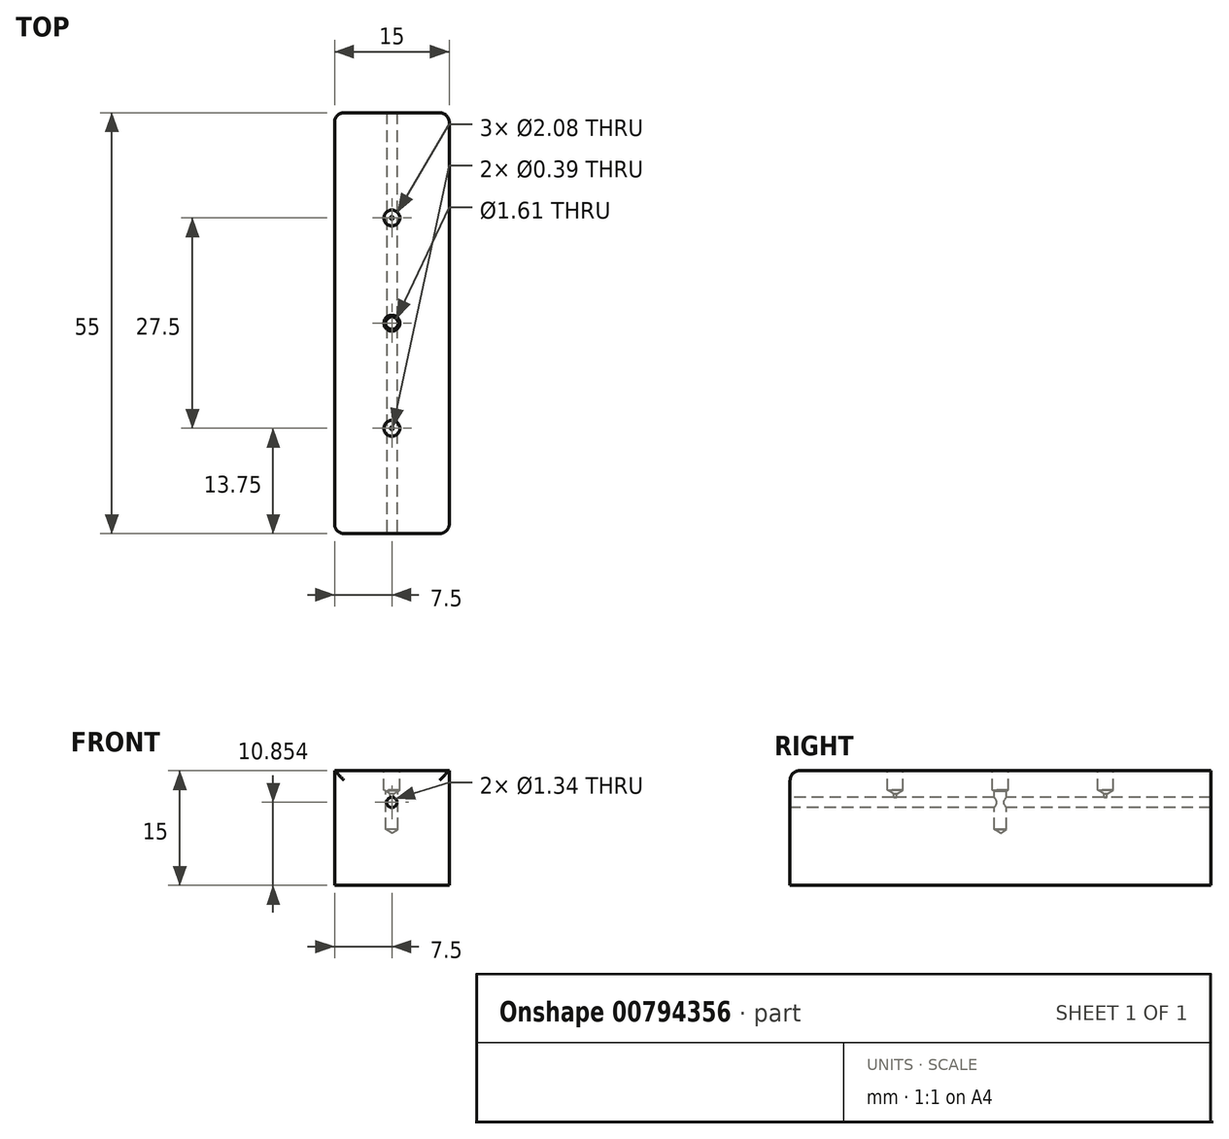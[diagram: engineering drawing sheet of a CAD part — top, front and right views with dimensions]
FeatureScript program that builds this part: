
annotation { "Feature Type Name" : "Feature", "Feature Type Description" : "" }
export const myFeature = defineFeature(function(context is Context, id is Id, definition is map)
    precondition{}
    {
        {
            var Q0;
            Q0=qCreatedBy(makeId("Front.planeOp"),FACE);
            var sketch = newSketch(context, id + "F0", { "sketchPlane" : qUnion([Q0])});
            skLineSegment(sketch, "E0.bottom", {"start": v(-15, 15) * mm, "end": v(0, 15) * mm});
            skLineSegment(sketch, "E0.top", {"start": v(-15, 0) * mm, "end": v(0, 0) * mm});
            skLineSegment(sketch, "E0.left", {"start": v(-15, 15) * mm, "end": v(-15, 0) * mm});
            skLineSegment(sketch, "E0.right", {"start": v(0, 15) * mm, "end": v(0, 0) * mm});
            skSolve(sketch);
        }
        {
            var Q0;
            Q0=makeQuery(id+"F0.imprint","IMPRINT",FACE,{"disambiguationData":[TD([[makeQuery(id+"F0.imprint","IMPRINT",EDGE,{"derivedFrom":sQuery(id+"F0.wireOp",EDGE,"E0.bottom")}),-1.0]])]});
            extrude(context, id + "F1", {"entities" : qUnion([Q0]), "depth" : 55 * mm, "offsetDistance" : 25 * mm});
        }
        {
            var Q0;
            Q0=makeQuery(id+"F1.opExtrude","SWEPT_FACE",FACE,{"disambiguationData":[OSD([sQuery(id+"F0.wireOp",EDGE,"E0.bottom")])]});
            var sketch = newSketch(context, id + "F2", { "sketchPlane" : qUnion([Q0])});
            skLineSegment(sketch, "E1", {"start": v(-7.5, -55) * mm, "end": v(-7.5, 0) * mm});
            skLineSegment(sketch, "E2", {"start": v(-15, -27.5) * mm, "end": v(0, -27.5) * mm});
            skLineSegment(sketch, "E3", {"start": v(-15, -55) * mm, "end": v(-15, -27.5) * mm});
            skLineSegment(sketch, "E4", {"start": v(0, -55) * mm, "end": v(0, -27.5) * mm});
            skLineSegment(sketch, "E5", {"start": v(-15, -27.5) * mm, "end": v(-15, 0) * mm});
            skLineSegment(sketch, "E6", {"start": v(-15, 0) * mm, "end": v(0, 0) * mm});
            skLineSegment(sketch, "E7", {"start": v(0, 0) * mm, "end": v(0, -27.5) * mm});
            skLineSegment(sketch, "E8", {"start": v(-15, -41.25) * mm, "end": v(0, -41.25) * mm});
            skLineSegment(sketch, "E9", {"start": v(-15, -13.75) * mm, "end": v(0, -13.75) * mm});
            skCircle(sketch, "E10", {"center": v(-7.5, -41.25) * mm, "radius": 0.9 * mm});
            skCircle(sketch, "E11", {"center": v(-7.5, -27.5) * mm, "radius": 0.9 * mm});
            skCircle(sketch, "E12", {"center": v(-7.5, -13.75) * mm, "radius": 0.9 * mm});
            skSolve(sketch);
        }
        {
            var Q0;
            Q0=sQuery(id+"F2.wireOp",VERTEX,"E10.center");
            var Q1;
            Q1=sQuery(id+"F2.wireOp",VERTEX,"E11.center");
            var Q2;
            Q2=sQuery(id+"F2.wireOp",VERTEX,"E12.center");
            var Q3;
            Q3=makeQuery(id+"F1.opExtrude","SWEPT_BODY",BODY,{"disambiguationData":[OSD([sQuery(id+"F0.wireOp",EDGE,"E0.bottom"),sQuery(id+"F0.wireOp",EDGE,"E0.top"),sQuery(id+"F0.wireOp",EDGE,"E0.left"),sQuery(id+"F0.wireOp",EDGE,"E0.right")])]});
            hole(context, id + "F3", {"style" : HoleStyle.SIMPLE, "endStyle" : HoleEndStyle.BLIND, "standardTappedOrClearance" : lookupTablePath({ "standard" : "ANSI", "engagement" : "75%", "pitch" : "56 tpi", "size" : "#3", "type" : "Tapped" }), "standardBlindInLast" : lookupTablePath({ "standard" : "ANSI", "engagement" : "75%", "pitch" : "56 tpi", "size" : "#3", "type" : "Tapped" }), "holeDiameter" : 2.08 * mm, "majorDiameter" : 2.5 * mm, "showTappedDepth" : true, "holeDepth" : 2.54 * mm, "isTappedThrough" : true, "tappedDepth" : 1.18 * mm, "tapClearance" : 3, "locations" : qUnion([Q0, Q1, Q2]), "scope" : qUnion([Q3])});
        }
        {
            var Q0;
            Q0=sQuery(id+"F2.wireOp",VERTEX,"E11.center");
            var Q1;
            Q1=sQuery(id+"F2.wireOp",VERTEX,"E12.center");
            var Q2;
            Q2=sQuery(id+"F2.wireOp",VERTEX,"E10.center");
            var Q3;
            Q3=makeQuery(id+"F1.opExtrude","SWEPT_BODY",BODY,{"disambiguationData":[OSD([sQuery(id+"F0.wireOp",EDGE,"E0.bottom"),sQuery(id+"F0.wireOp",EDGE,"E0.top"),sQuery(id+"F0.wireOp",EDGE,"E0.left"),sQuery(id+"F0.wireOp",EDGE,"E0.right")])]});
            hole(context, id + "F4", {"style" : HoleStyle.SIMPLE, "endStyle" : HoleEndStyle.BLIND, "holeDiameter" : 0.4 * mm, "majorDiameter" : 2.5 * mm, "holeDepth" : 0.89 * mm, "isTappedThrough" : true, "tappedDepth" : 1.18 * mm, "tapClearance" : 3, "locations" : qUnion([Q0, Q1, Q2]), "scope" : qUnion([Q3])});
        }
        {
            var Q0;
            Q0=makeQuery(id+"F1.opExtrude","CAP_FACE",FACE,{"disambiguationData":[OSD([sQuery(id+"F0.wireOp",EDGE,"E0.bottom"),sQuery(id+"F0.wireOp",EDGE,"E0.top"),sQuery(id+"F0.wireOp",EDGE,"E0.left"),sQuery(id+"F0.wireOp",EDGE,"E0.right")])],"isStart":false});
            var sketch = newSketch(context, id + "F5", { "sketchPlane" : qUnion([Q0])});
            skLineSegment(sketch, "E13", {"start": v(-7.5, 15) * mm, "end": v(-7.5, 10.85) * mm});
            skCircle(sketch, "E14", {"center": v(-7.5, 10.85) * mm, "radius": 0.67 * mm});
            skSolve(sketch);
        }
        {
            var Q0;
            Q0=makeQuery(id+"F5.imprint","IMPRINT",FACE,{"disambiguationData":[TD([[makeQuery(id+"F5.imprint","IMPRINT",EDGE,{"derivedFrom":sQuery(id+"F5.wireOp",EDGE,"E14")}),1.0]])]});
            var Q1;
            Q1=sQuery(id+"F5.wireOp",EDGE,"E14");
            extrude(context, id + "F6", {"entities" : qUnion([Q0]), "operationType" : NewBodyOperationType.REMOVE, "surfaceEntities" : qUnion([Q1]), "oppositeDirection" : true, "depth" : 58 * mm, "offsetDistance" : 25 * mm});
        }
        {
            var Q0;
            Q0=makeQuery(id+"F1.opExtrude","CAP_EDGE",EDGE,{"disambiguationData":[OSD([sQuery(id+"F0.wireOp",EDGE,"E0.bottom")])],"isStart":false});
            var Q1;
            Q1=makeQuery(id+"F1.opExtrude","CAP_EDGE",EDGE,{"disambiguationData":[OSD([sQuery(id+"F0.wireOp",EDGE,"E0.right")])],"isStart":true});
            var Q2;
            Q2=makeQuery(id+"F1.opExtrude","CAP_EDGE",EDGE,{"disambiguationData":[OSD([sQuery(id+"F0.wireOp",EDGE,"E0.left")])],"isStart":true});
            var Q3;
            Q3=makeQuery(id+"F1.opExtrude","CAP_EDGE",EDGE,{"disambiguationData":[OSD([sQuery(id+"F0.wireOp",EDGE,"E0.left")])],"isStart":false});
            var Q4;
            Q4=makeQuery(id+"F1.opExtrude","CAP_EDGE",EDGE,{"disambiguationData":[OSD([sQuery(id+"F0.wireOp",EDGE,"E0.right")])],"isStart":false});
            fillet(context, id + "F7", {"entities" : qUnion([Q0, Q1, Q2, Q3, Q4]), "radius" : 1.25 * mm, "tangentPropagation" : true, "allowEdgeOverflow" : false});
        }
        {
            var Q0;
            Q0=sQuery(id+"F2.wireOp",VERTEX,"E11.center");
            var Q1;
            Q1=makeQuery(id+"F1.opExtrude","SWEPT_BODY",BODY,{"disambiguationData":[OSD([sQuery(id+"F0.wireOp",EDGE,"E0.bottom"),sQuery(id+"F0.wireOp",EDGE,"E0.top"),sQuery(id+"F0.wireOp",EDGE,"E0.left"),sQuery(id+"F0.wireOp",EDGE,"E0.right")])]});
            hole(context, id + "F8", {"style" : HoleStyle.SIMPLE, "endStyle" : HoleEndStyle.BLIND, "standardTappedOrClearance" : lookupTablePath({ "standard" : "ANSI", "size" : "#52 (0.06)", "type" : "Drilled" }), "standardBlindInLast" : lookupTablePath({ "standard" : "ANSI", "size" : "#52", "type" : "Drilled" }), "holeDiameter" : 1.61 * mm, "majorDiameter" : 6.35 * mm, "holeDepth" : 5 * mm, "isTappedThrough" : true, "tappedDepth" : 1.18 * mm, "tapClearance" : 3, "locations" : qUnion([Q0]), "scope" : qUnion([Q1])});
        }
    });
